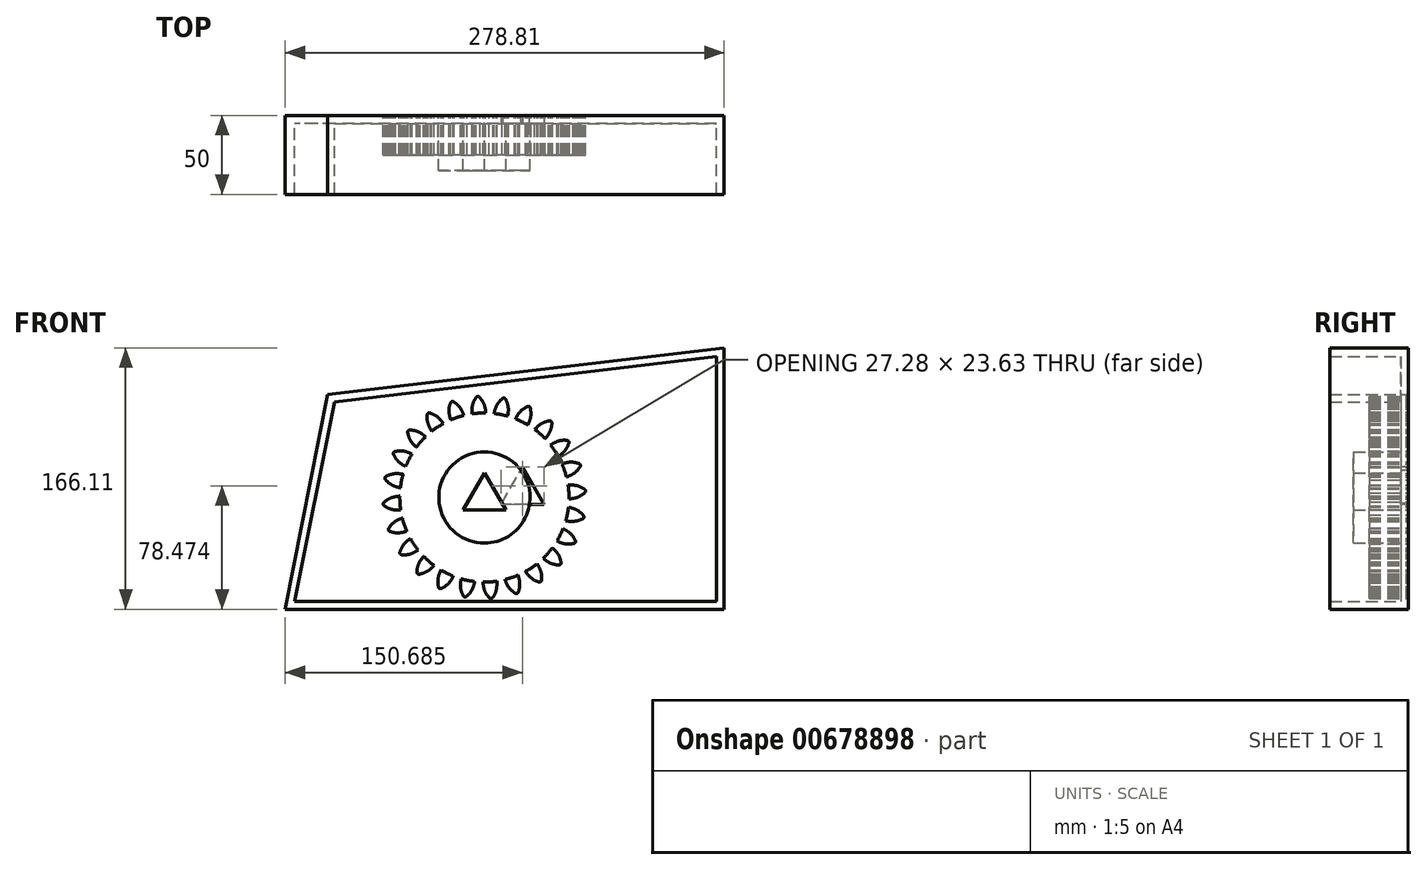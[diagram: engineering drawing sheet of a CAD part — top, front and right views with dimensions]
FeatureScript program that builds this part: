
annotation { "Feature Type Name" : "Feature", "Feature Type Description" : "" }
export const myFeature = defineFeature(function(context is Context, id is Id, definition is map)
    precondition{}
    {
        {
            var Q0;
            Q0=qCreatedBy(makeId("Front.planeOp"),FACE);
            var sketch = newSketch(context, id + "F0", { "sketchPlane" : qUnion([Q0])});
            skCircle(sketch, "E0", {"center": v(0, 0) * mm, "radius": 53.72 * mm});
            skCircle(sketch, "E1", {"center": v(0, 0) * mm, "radius": 63.5 * mm, "construction": true});
            skCircle(sketch, "E2", {"center": v(0, 0) * mm, "radius": 58.67 * mm, "construction": true});
            skLineSegment(sketch, "E3", {"start": v(0, 0) * mm, "end": v(0, 73.73) * mm, "construction": true});
            skLineSegment(sketch, "E4", {"start": v(0, 0) * mm, "end": v(-5.07, 77.32) * mm, "construction": true});
            skLineSegment(sketch, "E5", {"start": v(0, 58.67) * mm, "end": v(-93.6, 58.67) * mm, "construction": true});
            skLineSegment(sketch, "E6", {"start": v(0, 58.67) * mm, "end": v(-94.94, 24.12) * mm, "construction": true});
            skCircle(sketch, "E7", {"center": v(-13.72, 53.68) * mm, "radius": 14.6 * mm, "construction": true});
            skCircle(sketch, "E8", {"center": v(0, 0) * mm, "radius": 55.14 * mm, "construction": true});
            skArc(sketch, "E9", {"start": v(0, 58.67) * mm, "mid": v(-1.2, 61.2) * mm, "end": v(-2.86, 63.44) * mm});
            skArc(sketch, "E10", {"start": v(0.88, 53.71) * mm, "mid": v(0.6, 56.22) * mm, "end": v(0, 58.67) * mm});
            skArc(sketch, "E11.MirrorCS", {"start": v(-7.88, 53.14) * mm, "mid": v(-7.93, 55.66) * mm, "end": v(-7.66, 58.17) * mm});
            skCircle(sketch, "E12.MirrorC", {"center": v(6.6, 55.01) * mm, "radius": 14.6 * mm, "construction": true});
            skArc(sketch, "E13", {"start": v(-5.45, 63.27) * mm, "mid": v(-6.83, 60.84) * mm, "end": v(-7.66, 58.17) * mm});
            skArc(sketch, "E14", {"start": v(-2.86, 63.44) * mm, "mid": v(-4.2, 64.22) * mm, "end": v(-5.45, 63.27) * mm});
            skCircle(sketch, "E15", {"center": v(0, 0) * mm, "radius": 28.97 * mm});
            skCircle(sketch, "E16.cCircle", {"center": v(0, 0) * mm, "radius": 15.75 * mm, "construction": true});
            skLineSegment(sketch, "E16.0", {"start": v(0, 15.75) * mm, "end": v(13.64, -7.88) * mm});
            skLineSegment(sketch, "E16.1", {"start": v(13.64, -7.88) * mm, "end": v(-13.64, -7.88) * mm});
            skLineSegment(sketch, "E16.2", {"start": v(-13.64, -7.88) * mm, "end": v(0, 15.75) * mm});
            skSolve(sketch);
        }
        {
            var Q0;
            {var subQ0=sQuery(id+"F0.wireOp",EDGE,"E0");var subQ1=makeQuery(id+"F0.imprint","INTERSECT",VERTEX,{"derivedFrom":[subQ0,sQuery(id+"F0.wireOp",EDGE,"E10")]});Q0=makeQuery(id+"F0.imprint","IMPRINT",FACE,{"disambiguationData":[TD([[makeQuery(id+"F0.imprint","IMPRINT",EDGE,{"disambiguationData":[TD([[subQ1,1.0]])],"derivedFrom":subQ0}),-1.0]])]});}
            var Q1;
            Q1=makeQuery(id+"F0.imprint","IMPRINT",FACE,{"disambiguationData":[TD([[makeQuery(id+"F0.imprint","IMPRINT",EDGE,{"derivedFrom":sQuery(id+"F0.wireOp",EDGE,"E9")}),1.0]])]});
            extrude(context, id + "F1", {"entities" : qUnion([Q0, Q1]), "depth" : 25 * mm, "offsetDistance" : 25 * mm});
        }
        {
            var Q0;
            Q0=makeQuery(id+"F1.opExtrude","SWEPT_BODY",BODY,{"disambiguationData":[OSD([sQuery(id+"F0.wireOp",EDGE,"E0"),sQuery(id+"F0.wireOp",EDGE,"E9"),sQuery(id+"F0.wireOp",EDGE,"E10"),sQuery(id+"F0.wireOp",EDGE,"E11.MirrorCS"),sQuery(id+"F0.wireOp",EDGE,"E13"),sQuery(id+"F0.wireOp",EDGE,"E14")])]});
            var Q1;
            Q1=makeQuery(id+"F1.opExtrude","SWEPT_FACE",FACE,{"disambiguationData":[OSD([sQuery(id+"F0.wireOp",EDGE,"E0")])]});
            circularPattern(context, id + "F2", {"entities" : qUnion([Q0]), "axis" : qUnion([Q1]), "angle" : 360 * degree, "instanceCount" : 24, "equalSpace" : true});
        }
        {
            var Q0;
            Q0=makeQuery(id+"F0.imprint","IMPRINT",FACE,{"disambiguationData":[TD([[makeQuery(id+"F0.imprint","IMPRINT",EDGE,{"derivedFrom":sQuery(id+"F0.wireOp",EDGE,"E15")}),1.0]])]});
            extrude(context, id + "F3", {"entities" : qUnion([Q0]), "operationType" : NewBodyOperationType.ADD, "depth" : 35 * mm, "offsetDistance" : 25 * mm});
        }
        {
            var Q0;
            Q0=qCreatedBy(makeId("Front.planeOp"),FACE);
            var sketch = newSketch(context, id + "F4", { "sketchPlane" : qUnion([Q0])});
            skLineSegment(sketch, "E17", {"start": v(-99.47, 65.3) * mm, "end": v(152.3, 95.09) * mm});
            skLineSegment(sketch, "E18", {"start": v(152.3, 95.09) * mm, "end": v(152.3, -71.02) * mm});
            skLineSegment(sketch, "E19", {"start": v(152.3, -71.02) * mm, "end": v(-126.52, -71.02) * mm});
            skLineSegment(sketch, "E20", {"start": v(-99.47, 65.3) * mm, "end": v(-126.52, -71.02) * mm});
            skSolve(sketch);
        }
        {
            var Q0;
            Q0=makeQuery(id+"F4.imprint","IMPRINT",FACE,{"disambiguationData":[TD([[makeQuery(id+"F4.imprint","IMPRINT",EDGE,{"derivedFrom":sQuery(id+"F4.wireOp",EDGE,"E17")}),-1.0]])]});
            extrude(context, id + "F5", {"entities" : qUnion([Q0]), "depth" : 50 * mm, "offsetDistance" : 25 * mm});
        }
        {
            var Q0;
            Q0=makeQuery(id+"F5.opExtrude","CAP_FACE",FACE,{"disambiguationData":[OSD([sQuery(id+"F4.wireOp",EDGE,"E17"),sQuery(id+"F4.wireOp",EDGE,"E18"),sQuery(id+"F4.wireOp",EDGE,"E19"),sQuery(id+"F4.wireOp",EDGE,"E20")])],"isStart":false});
            shell(context, id + "F6", {"entities" : qUnion([Q0]), "thickness" : 5 * mm});
        }
        {
            var Q0;
            Q0=makeQuery(id+"F6.opShell","OFFSET_FACE",FACE,{"disambiguationData":[OSD([sQuery(id+"F4.wireOp",EDGE,"E17"),sQuery(id+"F4.wireOp",EDGE,"E18"),sQuery(id+"F4.wireOp",EDGE,"E19"),sQuery(id+"F4.wireOp",EDGE,"E20")])]});
            var sketch = newSketch(context, id + "F7", { "sketchPlane" : qUnion([Q0])});
            skLineSegment(sketch, "E21.0", {"start": v(24.16, 19.27) * mm, "end": v(37.8, -4.36) * mm});
            skLineSegment(sketch, "E21.1", {"start": v(37.8, -4.36) * mm, "end": v(10.52, -4.36) * mm});
            skLineSegment(sketch, "E21.2", {"start": v(10.52, -4.36) * mm, "end": v(24.16, 19.27) * mm});
            skSolve(sketch);
        }
        {
            var Q0;
            Q0=makeQuery(id+"F7.imprint","IMPRINT",FACE,{"disambiguationData":[TD([[makeQuery(id+"F7.imprint","IMPRINT",EDGE,{"derivedFrom":sQuery(id+"F7.wireOp",EDGE,"E21.0")}),-1.0]])]});
            extrude(context, id + "F8", {"entities" : qUnion([Q0]), "operationType" : NewBodyOperationType.REMOVE, "oppositeDirection" : true, "depth" : 30 * mm, "offsetDistance" : 25 * mm});
        }
    });
